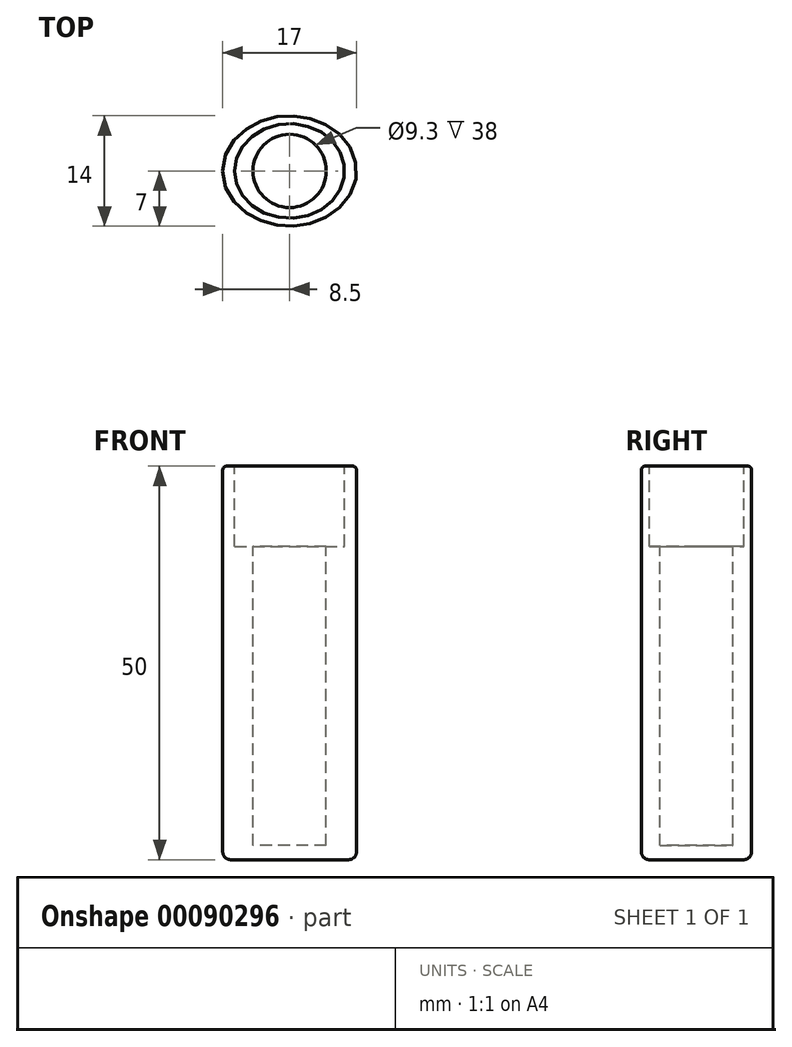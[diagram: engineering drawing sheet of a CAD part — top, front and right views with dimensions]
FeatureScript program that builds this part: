
annotation { "Feature Type Name" : "Feature", "Feature Type Description" : "" }
export const myFeature = defineFeature(function(context is Context, id is Id, definition is map)
    precondition{}
    {
        {
            var Q0;
            Q0=qCreatedBy(makeId("Top.planeOp"),FACE);
            var sketch = newSketch(context, id + "F0", { "sketchPlane" : qUnion([Q0])});
            skEllipse(sketch, "E0", {"center": v(0, 0) * mm, "majorRadius": 8.5 * mm, "minorRadius": 7 * mm, "majorAxis": v(-1, 0)});
            skCircle(sketch, "E1", {"center": v(0, 0) * mm, "radius": 4.55 * mm});
            skSolve(sketch);
        }
        {
            var Q0;
            Q0=makeQuery(id+"F0.imprint","IMPRINT",FACE,{"disambiguationData":[TD([[makeQuery(id+"F0.imprint","IMPRINT",EDGE,{"derivedFrom":sQuery(id+"F0.wireOp",EDGE,"E0")}),1.0]])]});
            var Q1;
            Q1=makeQuery(id+"F0.imprint","IMPRINT",FACE,{"disambiguationData":[TD([[makeQuery(id+"F0.imprint","IMPRINT",EDGE,{"derivedFrom":sQuery(id+"F0.wireOp",EDGE,"E1")}),1.0]])]});
            extrude(context, id + "F1", {"entities" : qUnion([Q0, Q1]), "depth" : 50 * mm});
        }
        {
            var Q0;
            Q0=makeQuery(id+"F1.opExtrude","CAP_FACE",FACE,{"disambiguationData":[OSD([sQuery(id+"F0.wireOp",EDGE,"E0")])],"isStart":false});
            var sketch = newSketch(context, id + "F2", { "sketchPlane" : qUnion([Q0])});
            skEllipse(sketch, "E2", {"center": v(0, 0) * mm, "majorRadius": 7 * mm, "minorRadius": 6 * mm, "majorAxis": v(-1, 0)});
            skSolve(sketch);
        }
        {
            var Q0;
            Q0=makeQuery(id+"F2.imprint","IMPRINT",FACE,{"disambiguationData":[TD([[makeQuery(id+"F2.imprint","IMPRINT",EDGE,{"derivedFrom":sQuery(id+"F2.wireOp",EDGE,"E2")}),1.0]])]});
            extrude(context, id + "F3", {"entities" : qUnion([Q0]), "operationType" : NewBodyOperationType.REMOVE, "oppositeDirection" : true, "depth" : 10.2 * mm});
        }
        {
            var Q0;
            Q0=makeQuery(id+"F3.boolean.opBoolean","COPY",FACE,{"derivedFrom":makeQuery(id+"F3.opExtrude","CAP_FACE",FACE,{"disambiguationData":[OSD([sQuery(id+"F2.wireOp",EDGE,"E2")])],"isStart":false})});
            var sketch = newSketch(context, id + "F4", { "sketchPlane" : qUnion([Q0])});
            skCircle(sketch, "E3", {"center": v(0, 0) * mm, "radius": 4.65 * mm});
            skSolve(sketch);
        }
        {
            var Q0;
            Q0=makeQuery(id+"F4.imprint","IMPRINT",FACE,{"disambiguationData":[TD([[makeQuery(id+"F4.imprint","IMPRINT",EDGE,{"derivedFrom":sQuery(id+"F4.wireOp",EDGE,"E3")}),1.0]])]});
            var Q1;
            Q1=sQuery(id+"F4.wireOp",EDGE,"E3");
            extrude(context, id + "F5", {"entities" : qUnion([Q0]), "operationType" : NewBodyOperationType.REMOVE, "surfaceEntities" : qUnion([Q1]), "oppositeDirection" : true, "depth" : 38 * mm});
        }
        {
            var Q0;
            Q0=makeQuery(id+"F5.boolean.opBoolean","COPY",EDGE,{"derivedFrom":makeQuery(id+"F5.opExtrude","CAP_EDGE",EDGE,{"disambiguationData":[OSD([sQuery(id+"F4.wireOp",EDGE,"E3")])],"isStart":true})});
            var Q1;
            Q1=makeQuery(id+"F3.boolean.opBoolean","COPY",EDGE,{"derivedFrom":makeQuery(id+"F3.opExtrude","CAP_EDGE",EDGE,{"disambiguationData":[OSD([sQuery(id+"F2.wireOp",EDGE,"E2")])],"isStart":true})});
            var Q2;
            Q2=makeQuery(id+"F1.opExtrude","CAP_EDGE",EDGE,{"disambiguationData":[OSD([sQuery(id+"F0.wireOp",EDGE,"E0")])],"isStart":false});
            fillet(context, id + "F6", {"entities" : qUnion([Q0, Q1, Q2]), "radius" : .5 * mm, "tangentPropagation" : true, "allowEdgeOverflow" : false});
        }
        {
            var Q0;
            Q0=makeQuery(id+"F1.opExtrude","CAP_EDGE",EDGE,{"disambiguationData":[OSD([sQuery(id+"F0.wireOp",EDGE,"E0")])],"isStart":true});
            fillet(context, id + "F7", {"entities" : qUnion([Q0]), "radius" : 1 * mm, "tangentPropagation" : true, "allowEdgeOverflow" : false});
        }
    });
